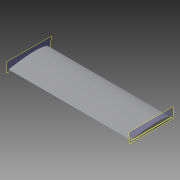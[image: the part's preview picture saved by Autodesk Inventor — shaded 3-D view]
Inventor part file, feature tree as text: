
AUTODESK INVENTOR PART (.ipt)
format: ipt  version: 2015 (Build 190159000, 159)  size: 89,088 bytes
history: native  units: in
note: dims shown in document units (in); Inventor stores cm internally (conversion verified against a paired STEP export)
features: other x3, plane x3, sketch x2
ambient origin geometry x8: Origin, YZ Plane, XZ Plane, XY Plane, X Axis, Y Axis, Z Axis, Center Point
bodies: Solid1 (feature_tree)
feature tree (8):
  other  "Generic Wing 1.ipt"
  other  "Solid1::Generic Wing 1.ipt"
  other  "TaggingFeature1"
  sketch  "Sketch1"  dims[d0=0.3937in]
  sketch  "Sketch2"
  plane  "Work Plane1"
  plane  "Work Plane2"
  plane  "Work Plane3"
